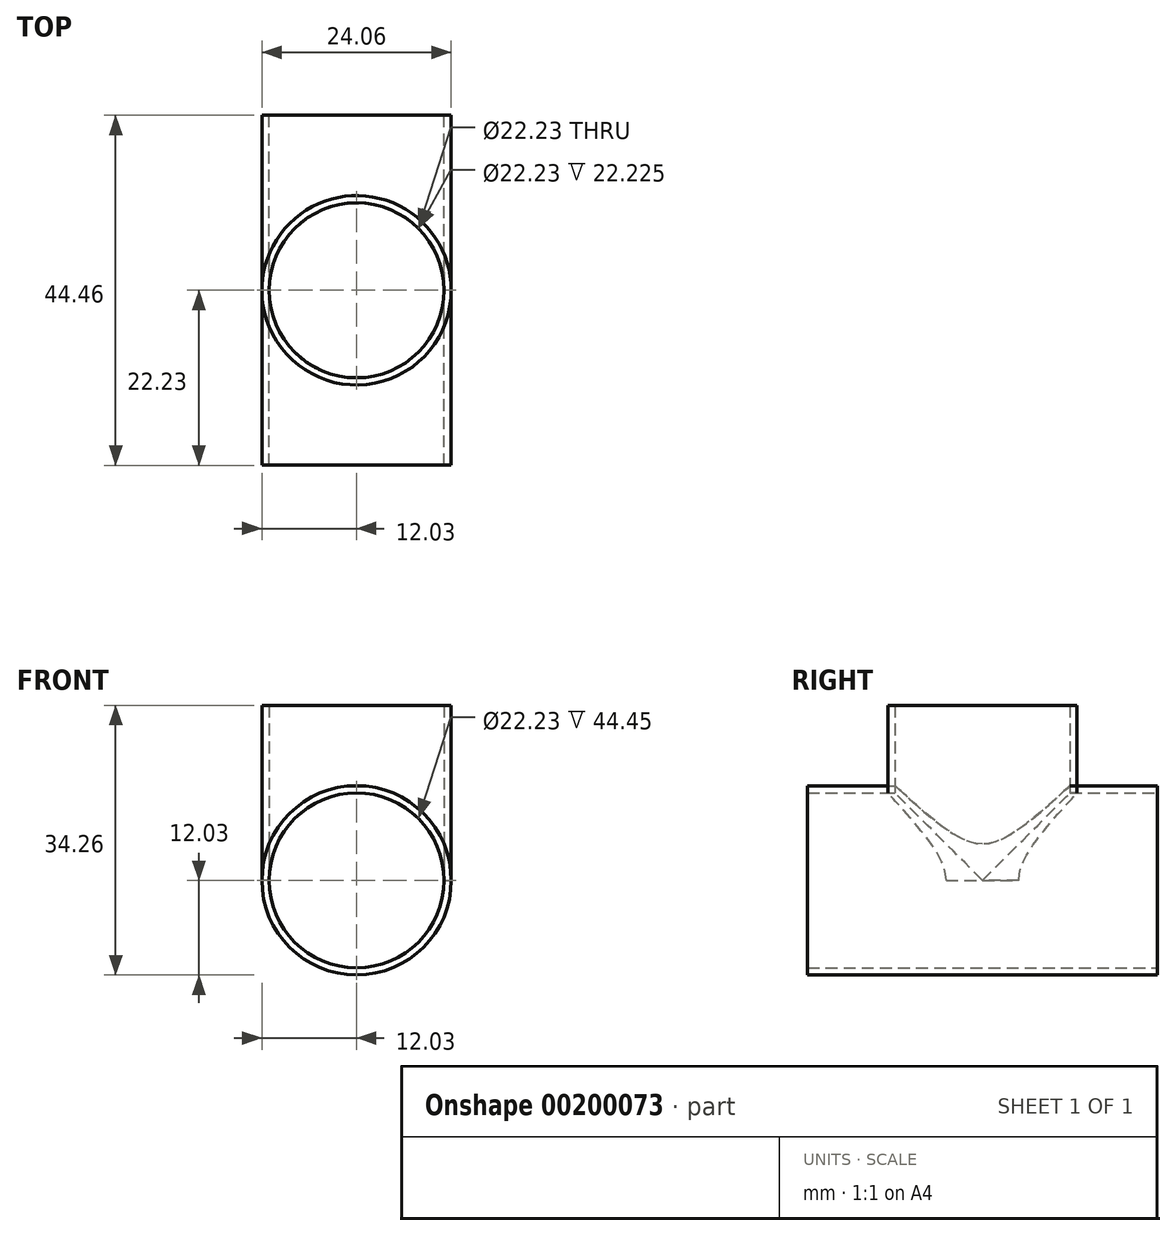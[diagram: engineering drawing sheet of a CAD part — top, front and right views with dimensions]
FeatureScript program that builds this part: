
annotation { "Feature Type Name" : "Feature", "Feature Type Description" : "" }
export const myFeature = defineFeature(function(context is Context, id is Id, definition is map)
    precondition{}
    {
        {
            var Q0;
            Q0=qCreatedBy(makeId("Front.planeOp"),FACE);
            var sketch = newSketch(context, id + "F0", { "sketchPlane" : qUnion([Q0])});
            skCircle(sketch, "E0", {"center": v(0, 0) * mm, "radius": 11.11 * mm});
            skCircle(sketch, "E1", {"center": v(0, 0) * mm, "radius": 12.03 * mm});
            skSolve(sketch);
        }
        {
            var Q0;
            Q0=qCreatedBy(makeId("Top.planeOp"),FACE);
            var sketch = newSketch(context, id + "F1", { "sketchPlane" : qUnion([Q0])});
            skCircle(sketch, "E2", {"center": v(0, 0) * mm, "radius": 12.03 * mm});
            skCircle(sketch, "E3", {"center": v(0, 0) * mm, "radius": 11.11 * mm});
            skSolve(sketch);
        }
        {
            var Q0;
            Q0=makeQuery(id+"F0.imprint","IMPRINT",FACE,{"disambiguationData":[TD([[makeQuery(id+"F0.imprint","IMPRINT",EDGE,{"derivedFrom":sQuery(id+"F0.wireOp",EDGE,"E0")}),-1.0]])]});
            extrude(context, id + "F2", {"entities" : qUnion([Q0]), "depth" : 22.22 * mm, "hasSecondDirection" : true, "secondDirectionOppositeDirection" : true, "secondDirectionDepth" : 22.22 * mm});
        }
        {
            var Q0;
            Q0=makeQuery(id+"F1.imprint","IMPRINT",FACE,{"disambiguationData":[TD([[makeQuery(id+"F1.imprint","IMPRINT",EDGE,{"derivedFrom":sQuery(id+"F1.wireOp",EDGE,"E2")}),1.0]])]});
            var Q1;
            Q1=sQuery(id+"F1.wireOp",EDGE,"E2");
            var Q2;
            Q2=sQuery(id+"F1.wireOp",EDGE,"E3");
            extrude(context, id + "F3", {"entities" : qUnion([Q0]), "surfaceEntities" : qUnion([Q1, Q2]), "depth" : 22.22 * mm});
        }
        {
            var Q0;
            Q0=sQuery(id+"F1.wireOp",VERTEX,"E3.center");
            var Q1;
            Q1=makeQuery(id+"F2.opExtrude","SWEPT_BODY",BODY,{"disambiguationData":[OSD([sQuery(id+"F0.wireOp",EDGE,"E0"),sQuery(id+"F0.wireOp",EDGE,"E1")])]});
            hole(context, id + "F4", {"style" : HoleStyle.SIMPLE, "endStyle" : HoleEndStyle.THROUGH, "oppositeDirection" : true, "holeDiameter" : 22.22 * mm, "locations" : qUnion([Q0]), "scope" : qUnion([Q1]), "isTappedThrough" : true});
        }
        {
            var Q0;
            Q0=sQuery(id+"F0.wireOp",VERTEX,"E0.center");
            var Q1;
            Q1=makeQuery(id+"F3.opExtrude","SWEPT_BODY",BODY,{"disambiguationData":[OSD([sQuery(id+"F1.wireOp",EDGE,"E2"),sQuery(id+"F1.wireOp",EDGE,"E3")])]});
            hole(context, id + "F5", {"style" : HoleStyle.SIMPLE, "endStyle" : HoleEndStyle.BLIND, "holeDiameter" : 22.22 * mm, "holeDepth" : 12.7 * mm, "locations" : qUnion([Q0]), "scope" : qUnion([Q1])});
        }
        {
            var Q0;
            Q0=sQuery(id+"F0.wireOp",VERTEX,"E0.center");
            var Q1;
            Q1=makeQuery(id+"F3.opExtrude","SWEPT_BODY",BODY,{"disambiguationData":[OSD([sQuery(id+"F1.wireOp",EDGE,"E2"),sQuery(id+"F1.wireOp",EDGE,"E3")])]});
            hole(context, id + "F6", {"style" : HoleStyle.SIMPLE, "endStyle" : HoleEndStyle.THROUGH, "oppositeDirection" : true, "holeDiameter" : 22.22 * mm, "startFromSketch" : true, "locations" : qUnion([Q0]), "scope" : qUnion([Q1]), "isTappedThrough" : true});
        }
    });
